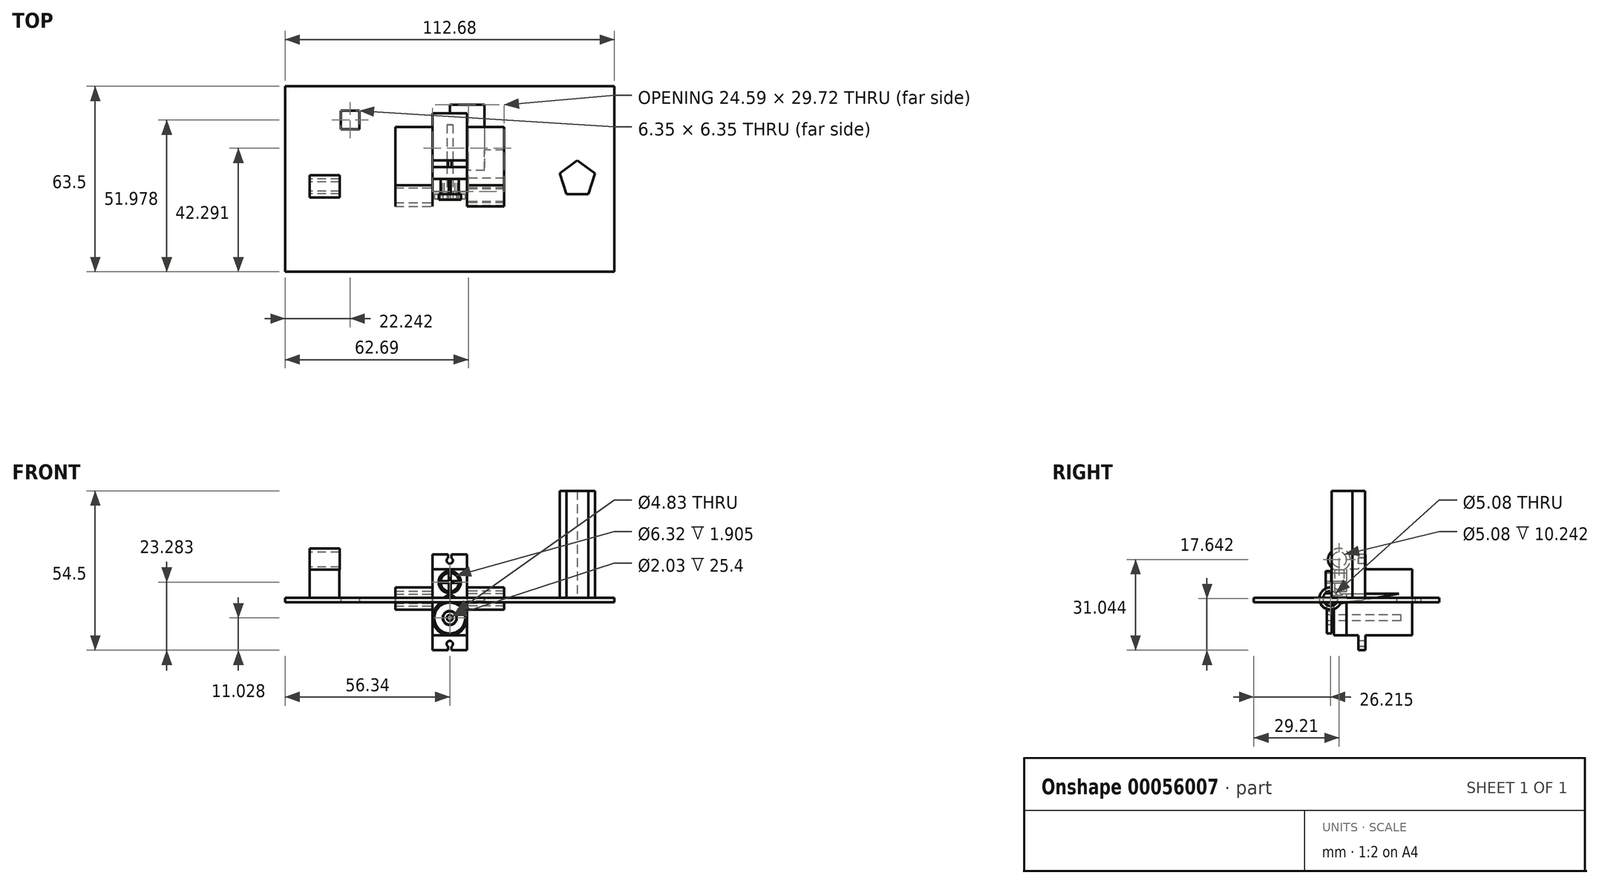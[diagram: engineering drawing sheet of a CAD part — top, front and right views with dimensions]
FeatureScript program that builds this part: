
annotation { "Feature Type Name" : "Feature", "Feature Type Description" : "" }
export const myFeature = defineFeature(function(context is Context, id is Id, definition is map)
    precondition{}
    {
        {
            var Q0;
            Q0=qCreatedBy(makeId("Top.planeOp"),FACE);
            var sketch = newSketch(context, id + "F0", { "sketchPlane" : qUnion([Q0])});
            skLineSegment(sketch, "E0.rect.bottom", {"start": v(56.34, 31.75) * mm, "end": v(-56.34, 31.75) * mm});
            skLineSegment(sketch, "E0.rect.top", {"start": v(56.34, -31.75) * mm, "end": v(-56.34, -31.75) * mm});
            skLineSegment(sketch, "E0.rect.left", {"start": v(56.34, 31.75) * mm, "end": v(56.34, -31.75) * mm});
            skLineSegment(sketch, "E0.rect.right", {"start": v(-56.34, 31.75) * mm, "end": v(-56.34, -31.75) * mm});
            skPoint(sketch, "E0.rect.middle", {"position": v(0, 0) * mm});
            skCircle(sketch, "E1.cCircle", {"center": v(43.64, 0) * mm, "radius": 5.14 * mm, "construction": true});
            skLineSegment(sketch, "E1.0", {"start": v(47.37, -5.14) * mm, "end": v(39.9, -5.14) * mm});
            skLineSegment(sketch, "E1.1", {"start": v(39.9, -5.14) * mm, "end": v(37.6, 1.96) * mm});
            skLineSegment(sketch, "E1.2", {"start": v(37.6, 1.96) * mm, "end": v(43.64, 6.35) * mm});
            skLineSegment(sketch, "E1.3", {"start": v(43.64, 6.35) * mm, "end": v(49.68, 1.96) * mm});
            skLineSegment(sketch, "E1.4", {"start": v(49.68, 1.96) * mm, "end": v(47.37, -5.14) * mm});
            skPoint(sketch, "E1.0.midPoint", {"position": v(43.64, -5.14) * mm});
            skLineSegment(sketch, "E2.bottom", {"start": v(0, 25.4) * mm, "end": v(11.89, 25.4) * mm});
            skLineSegment(sketch, "E2.top", {"start": v(0, 2.92) * mm, "end": v(11.89, 2.92) * mm});
            skLineSegment(sketch, "E2.left", {"start": v(0, 25.4) * mm, "end": v(0, 2.92) * mm});
            skLineSegment(sketch, "E2.right", {"start": v(11.89, 25.4) * mm, "end": v(11.89, 2.92) * mm});
            skLineSegment(sketch, "E3.bottom", {"start": v(-37.27, 23.4) * mm, "end": v(-30.92, 23.4) * mm});
            skLineSegment(sketch, "E3.top", {"start": v(-37.27, 17.05) * mm, "end": v(-30.92, 17.05) * mm});
            skLineSegment(sketch, "E3.left", {"start": v(-37.27, 23.4) * mm, "end": v(-37.27, 17.05) * mm});
            skLineSegment(sketch, "E3.right", {"start": v(-30.92, 23.4) * mm, "end": v(-30.92, 17.05) * mm});
            skLineSegment(sketch, "E4", {"start": v(5.94, 25.4) * mm, "end": v(5.94, 2.92) * mm});
            skLineSegment(sketch, "E5.rect.bottom", {"start": v(-37.73, -4.12) * mm, "end": v(-47.94, -4.12) * mm});
            skLineSegment(sketch, "E5.rect.top", {"start": v(-37.73, -0.96) * mm, "end": v(-47.94, -0.96) * mm});
            skLineSegment(sketch, "E5.rect.left", {"start": v(-37.73, -4.12) * mm, "end": v(-37.73, -0.96) * mm});
            skLineSegment(sketch, "E5.rect.right", {"start": v(-47.94, -4.12) * mm, "end": v(-47.94, -0.96) * mm});
            skPoint(sketch, "E5.rect.middle", {"position": v(-42.83, -2.54) * mm});
            skSolve(sketch);
        }
        {
            var Q0;
            Q0 = qSketchRegion(id + "F0", true);
            extrude(context, id + "F1", {"entities" : qUnion([Q0]), "depth" : 1.59 * mm});
        }
        {
            var Q0;
            Q0=makeQuery(id+"F0.imprint","IMPRINT",FACE,{"disambiguationData":[TD([[makeQuery(id+"F0.imprint","IMPRINT",EDGE,{"derivedFrom":sQuery(id+"F0.wireOp",EDGE,"E1.0")}),-1.0]])]});
            extrude(context, id + "F2", {"entities" : qUnion([Q0]), "operationType" : NewBodyOperationType.ADD, "depth" : 38.1 * mm});
        }
        {
            var Q0;
            Q0=qCreatedBy(makeId("Front.planeOp"),FACE);
            var sketch = newSketch(context, id + "F3", { "sketchPlane" : qUnion([Q0])});
            skLineSegment(sketch, "E6.rect.bottom", {"start": v(5.94, 11.32) * mm, "end": v(-5.94, 11.32) * mm});
            skLineSegment(sketch, "E6.rect.top", {"start": v(5.94, -11.32) * mm, "end": v(-5.94, -11.32) * mm});
            skLineSegment(sketch, "E6.rect.left", {"start": v(5.94, 11.32) * mm, "end": v(5.94, -11.32) * mm});
            skLineSegment(sketch, "E6.rect.right", {"start": v(-5.94, 11.32) * mm, "end": v(-5.94, -11.32) * mm});
            skPoint(sketch, "E6.rect.middle", {"position": v(0, 0) * mm});
            skCircle(sketch, "E7", {"center": v(0, -5.37) * mm, "radius": 5.94 * mm});
            skCircle(sketch, "E8", {"center": v(0, -5.37) * mm, "radius": 2.3 * mm});
            skCircle(sketch, "E9", {"center": v(0, 0) * mm, "radius": 2.45 * mm});
            skSolve(sketch);
        }
        {
            var Q0;
            {var subQ0=sQuery(id+"F3.wireOp",EDGE,"E9");var subQ1=sQuery(id+"F3.wireOp",EDGE,"E7");var subQ2=makeQuery(id+"F3.imprint","INTERSECT",VERTEX,{"disambiguationData":[OD(0.0)],"derivedFrom":[subQ1,subQ0]});Q0=makeQuery(id+"F3.imprint","IMPRINT",FACE,{"disambiguationData":[TD([[makeQuery(id+"F3.imprint","IMPRINT",EDGE,{"disambiguationData":[TD([[subQ2,-1.0]])],"derivedFrom":subQ1}),-1.0]])]});}
            var Q1;
            {var subQ0=sQuery(id+"F3.wireOp",EDGE,"E9");var subQ1=sQuery(id+"F3.wireOp",EDGE,"E7");var subQ2=makeQuery(id+"F3.imprint","INTERSECT",VERTEX,{"disambiguationData":[OD(0.0)],"derivedFrom":[subQ1,subQ0]});Q1=makeQuery(id+"F3.imprint","IMPRINT",FACE,{"disambiguationData":[TD([[makeQuery(id+"F3.imprint","IMPRINT",EDGE,{"disambiguationData":[TD([[subQ2,-1.0]])],"derivedFrom":subQ1}),1.0]])]});}
            var Q2;
            Q2=makeQuery(id+"F3.imprint","IMPRINT",FACE,{"disambiguationData":[TD([[makeQuery(id+"F3.imprint","IMPRINT",EDGE,{"derivedFrom":sQuery(id+"F3.wireOp",EDGE,"E8")}),1.0]])]});
            var Q3;
            Q3=makeQuery(id+"F3.imprint","IMPRINT",FACE,{"disambiguationData":[TD([[makeQuery(id+"F3.imprint","IMPRINT",EDGE,{"derivedFrom":sQuery(id+"F3.wireOp",EDGE,"E8")}),-1.0]])]});
            extrude(context, id + "F4", {"entities" : qUnion([Q0, Q1, Q2, Q3]), "depth" : 4.32 * mm});
        }
        {
            var Q0;
            Q0=makeQuery(id+"F3.imprint","IMPRINT",FACE,{"disambiguationData":[TD([[makeQuery(id+"F3.imprint","IMPRINT",EDGE,{"derivedFrom":sQuery(id+"F3.wireOp",EDGE,"E8")}),1.0]])]});
            extrude(context, id + "F5", {"entities" : qUnion([Q0]), "operationType" : NewBodyOperationType.ADD, "depth" : 6.76 * mm});
        }
        {
            var Q0;
            {var subQ0=sQuery(id+"F3.wireOp",EDGE,"E9");var subQ1=sQuery(id+"F3.wireOp",EDGE,"E7");var subQ2=makeQuery(id+"F3.imprint","INTERSECT",VERTEX,{"disambiguationData":[OD(0.0)],"derivedFrom":[subQ1,subQ0]});Q0=makeQuery(id+"F3.imprint","IMPRINT",FACE,{"disambiguationData":[TD([[makeQuery(id+"F3.imprint","IMPRINT",EDGE,{"disambiguationData":[TD([[subQ2,-1.0]])],"derivedFrom":subQ1}),1.0]])]});}
            var Q1;
            Q1=makeQuery(id+"F3.imprint","IMPRINT",FACE,{"disambiguationData":[TD([[makeQuery(id+"F3.imprint","IMPRINT",EDGE,{"derivedFrom":sQuery(id+"F3.wireOp",EDGE,"E8")}),-1.0]])]});
            var Q2;
            Q2=makeQuery(id+"F3.imprint","IMPRINT",FACE,{"disambiguationData":[TD([[makeQuery(id+"F3.imprint","IMPRINT",EDGE,{"derivedFrom":sQuery(id+"F3.wireOp",EDGE,"E8")}),1.0]])]});
            var Q3;
            {var subQ0=sQuery(id+"F3.wireOp",EDGE,"E6.rect.left");var subQ1=sQuery(id+"F3.wireOp",EDGE,"E6.rect.top");var subQ2=makeQuery(id+"F3.imprint","INTERSECT",VERTEX,{"derivedFrom":[subQ1,subQ0]});Q3=makeQuery(id+"F3.imprint","IMPRINT",FACE,{"disambiguationData":[TD([[makeQuery(id+"F3.imprint","IMPRINT",EDGE,{"disambiguationData":[TD([[subQ2,-1.0]])],"derivedFrom":subQ1}),-1.0]])]});}
            var Q4;
            {var subQ0=sQuery(id+"F3.wireOp",EDGE,"E6.rect.right");var subQ1=sQuery(id+"F3.wireOp",EDGE,"E6.rect.top");var subQ2=makeQuery(id+"F3.imprint","INTERSECT",VERTEX,{"derivedFrom":[subQ1,subQ0]});Q4=makeQuery(id+"F3.imprint","IMPRINT",FACE,{"disambiguationData":[TD([[makeQuery(id+"F3.imprint","IMPRINT",EDGE,{"disambiguationData":[TD([[subQ2,1.0]])],"derivedFrom":subQ1}),-1.0]])]});}
            var Q5;
            {var subQ1=sQuery(id+"F3.wireOp",EDGE,"E6.rect.bottom");Q5=makeQuery(id+"F3.imprint","IMPRINT",FACE,{"disambiguationData":[TD([[makeQuery(id+"F3.imprint","IMPRINT",EDGE,{"derivedFrom":subQ1}),1.0]])]});}
            var Q6;
            {var subQ0=sQuery(id+"F3.wireOp",EDGE,"E9");var subQ1=sQuery(id+"F3.wireOp",EDGE,"E7");var subQ2=makeQuery(id+"F3.imprint","INTERSECT",VERTEX,{"disambiguationData":[OD(0.0)],"derivedFrom":[subQ1,subQ0]});Q6=makeQuery(id+"F3.imprint","IMPRINT",FACE,{"disambiguationData":[TD([[makeQuery(id+"F3.imprint","IMPRINT",EDGE,{"disambiguationData":[TD([[subQ2,-1.0]])],"derivedFrom":subQ1}),-1.0]])]});}
            extrude(context, id + "F6", {"entities" : qUnion([Q0, Q1, Q2, Q3, Q4, Q5, Q6]), "operationType" : NewBodyOperationType.ADD, "oppositeDirection" : true, "depth" : 22.48 * mm});
        }
        {
            var Q0;
            Q0=makeQuery(id+"F6.opExtrude","SWEPT_FACE",FACE,{"disambiguationData":[OSD([sQuery(id+"F3.wireOp",EDGE,"E6.rect.bottom")])]});
            var sketch = newSketch(context, id + "F7", { "sketchPlane" : qUnion([Q0])});
            skLineSegment(sketch, "E10", {"start": v(-5.94, 4.06) * mm, "end": v(5.94, 4.06) * mm});
            skLineSegment(sketch, "E11", {"start": v(5.94, 4.06) * mm, "end": v(5.94, 6.4) * mm});
            skLineSegment(sketch, "E12", {"start": v(5.94, 6.4) * mm, "end": v(-5.94, 6.4) * mm});
            skLineSegment(sketch, "E13", {"start": v(-5.94, 6.4) * mm, "end": v(-5.94, 4.06) * mm});
            skSolve(sketch);
        }
        {
            var Q0;
            Q0=makeQuery(id+"F7.imprint","IMPRINT",FACE,{"disambiguationData":[TD([[makeQuery(id+"F7.imprint","IMPRINT",EDGE,{"derivedFrom":sQuery(id+"F7.wireOp",EDGE,"E10")}),1.0]])]});
            extrude(context, id + "F8", {"entities" : qUnion([Q0]), "operationType" : NewBodyOperationType.ADD, "depth" : 5.08 * mm});
        }
        {
            var Q0;
            Q0=makeQuery(id+"F8.opExtrude","SWEPT_FACE",FACE,{"disambiguationData":[OSD([sQuery(id+"F7.wireOp",EDGE,"E10")])]});
            var sketch = newSketch(context, id + "F9", { "sketchPlane" : qUnion([Q0])});
            skCircle(sketch, "E14", {"center": v(0, 14.29) * mm, "radius": 1.07 * mm});
            skLineSegment(sketch, "E15.bottom", {"start": v(-0.52, 16.4) * mm, "end": v(0.62, 16.4) * mm});
            skLineSegment(sketch, "E15.top", {"start": v(-0.52, 15) * mm, "end": v(0.62, 15) * mm});
            skLineSegment(sketch, "E15.left", {"start": v(-0.52, 16.4) * mm, "end": v(-0.52, 15) * mm});
            skLineSegment(sketch, "E15.right", {"start": v(0.62, 16.4) * mm, "end": v(0.62, 15) * mm});
            skSolve(sketch);
        }
        {
            var Q0;
            Q0 = qSketchRegion(id + "F9", true);
            extrude(context, id + "F10", {"entities" : qUnion([Q0]), "operationType" : NewBodyOperationType.REMOVE, "oppositeDirection" : true, "depth" : 2.48 * mm});
        }
        {
            var Q0;
            Q0=makeQuery(id+"F6.opExtrude","SWEPT_FACE",FACE,{"disambiguationData":[OSD([sQuery(id+"F3.wireOp",EDGE,"E6.rect.top")])]});
            var sketch = newSketch(context, id + "F11", { "sketchPlane" : qUnion([Q0])});
            skLineSegment(sketch, "E16", {"start": v(-5.94, -4.06) * mm, "end": v(5.94, -4.06) * mm});
            skLineSegment(sketch, "E17", {"start": v(5.94, -4.06) * mm, "end": v(5.94, -6.4) * mm});
            skLineSegment(sketch, "E18", {"start": v(5.94, -6.4) * mm, "end": v(-5.94, -6.4) * mm});
            skLineSegment(sketch, "E19", {"start": v(-5.94, -6.4) * mm, "end": v(-5.94, -4.06) * mm});
            skSolve(sketch);
        }
        {
            var Q0;
            Q0=makeQuery(id+"F11.imprint","IMPRINT",FACE,{"disambiguationData":[TD([[makeQuery(id+"F11.imprint","IMPRINT",EDGE,{"derivedFrom":sQuery(id+"F11.wireOp",EDGE,"E16")}),-1.0]])]});
            extrude(context, id + "F12", {"entities" : qUnion([Q0]), "operationType" : NewBodyOperationType.ADD, "depth" : 5.08 * mm});
        }
        {
            var Q0;
            Q0=makeQuery(id+"F12.opExtrude","SWEPT_FACE",FACE,{"disambiguationData":[OSD([sQuery(id+"F11.wireOp",EDGE,"E16")])]});
            var sketch = newSketch(context, id + "F13", { "sketchPlane" : qUnion([Q0])});
            skLineSegment(sketch, "E20", {"start": v(5.94, -16.4) * mm, "end": v(0.52, -16.4) * mm});
            skLineSegment(sketch, "E21", {"start": v(0.52, -16.4) * mm, "end": v(-0.62, -16.4) * mm});
            skLineSegment(sketch, "E22", {"start": v(0.52, -16.4) * mm, "end": v(0.52, -15.22) * mm});
            skArc(sketch, "E23", {"start": v(0.52, -15.22) * mm, "mid": v(0.06, -13.22) * mm, "end": v(-0.62, -15.15) * mm});
            skLineSegment(sketch, "E24", {"start": v(-0.62, -16.4) * mm, "end": v(-0.62, -15.15) * mm});
            skPoint(sketch, "E25.orphan", {"position": v(0.52, -15) * mm});
            skPoint(sketch, "E26.orphan", {"position": v(-0.62, -15) * mm});
            skSolve(sketch);
        }
        {
            var Q0;
            Q0 = qSketchRegion(id + "F13", true);
            extrude(context, id + "F14", {"entities" : qUnion([Q0]), "operationType" : NewBodyOperationType.REMOVE, "oppositeDirection" : true, "depth" : 25.4 * mm});
        }
        {
            var Q0;
            Q0=makeQuery(id+"F5.opExtrude","CAP_FACE",FACE,{"disambiguationData":[OSD([sQuery(id+"F3.wireOp",EDGE,"E8")])],"isStart":false});
            var sketch = newSketch(context, id + "F15", { "sketchPlane" : qUnion([Q0])});
            skCircle(sketch, "E27", {"center": v(0, -5.37) * mm, "radius": 1.02 * mm});
            skSolve(sketch);
        }
        {
            var Q0;
            Q0 = qSketchRegion(id + "F15", true);
            extrude(context, id + "F16", {"entities" : qUnion([Q0]), "operationType" : NewBodyOperationType.REMOVE, "oppositeDirection" : true, "depth" : 25.4 * mm});
        }
        {
            var Q0;
            {var subQ0=sQuery(id+"F3.wireOp",EDGE,"E6.rect.right");var subQ1=sQuery(id+"F3.wireOp",EDGE,"E6.rect.left");var subQ2=sQuery(id+"F3.wireOp",EDGE,"E6.rect.bottom");var subQ3=makeQuery(id+"F6.opExtrude","CAP_FACE",FACE,{"disambiguationData":[OSD([subQ2,sQuery(id+"F3.wireOp",EDGE,"E6.rect.top"),subQ1,subQ0])],"isStart":true});Q0=makeQuery(id+"F6.boolean.opBoolean","SPLIT",FACE,{"disambiguationData":[TD([makeQuery(id+"F4.opExtrude","SWEPT_FACE",FACE,{"disambiguationData":[OSD([sQuery(id+"F3.wireOp",EDGE,"E7")])]}),makeQuery(id+"F4.opExtrude","SWEPT_FACE",FACE,{"disambiguationData":[OSD([sQuery(id+"F3.wireOp",EDGE,"E9")])]}),makeQuery(id+"F6.opExtrude","SWEPT_FACE",FACE,{"disambiguationData":[OSD([subQ2])]}),subQ3,makeQuery(id+"F6.opExtrude","SWEPT_FACE",FACE,{"disambiguationData":[OSD([subQ1])]}),makeQuery(id+"F6.opExtrude","SWEPT_FACE",FACE,{"disambiguationData":[OSD([subQ0])]})])],"derivedFrom":subQ3});}
            var sketch = newSketch(context, id + "F17", { "sketchPlane" : qUnion([Q0])});
            skPoint(sketch, "E28.endSnap0", {"position": v(0, 2.45) * mm});
            skLineSegment(sketch, "E29", {"start": v(0, 10.05) * mm, "end": v(-0.32, 10.05) * mm});
            skLineSegment(sketch, "E30", {"start": v(0, 10.05) * mm, "end": v(0.32, 10.05) * mm});
            skLineSegment(sketch, "E31", {"start": v(-3.16, 6.88) * mm, "end": v(-3.16, 7.2) * mm});
            skLineSegment(sketch, "E32", {"start": v(-3.16, 6.88) * mm, "end": v(-3.16, 6.57) * mm});
            skLineSegment(sketch, "E33", {"start": v(-3.16, 7.2) * mm, "end": v(-0.32, 7.2) * mm});
            skLineSegment(sketch, "E34", {"start": v(-0.32, 7.2) * mm, "end": v(-0.32, 10.05) * mm});
            skLineSegment(sketch, "E35", {"start": v(0.32, 10.05) * mm, "end": v(0.32, 7.2) * mm});
            skLineSegment(sketch, "E36", {"start": v(0.32, 7.2) * mm, "end": v(3.16, 7.2) * mm});
            skLineSegment(sketch, "E37", {"start": v(3.16, 7.2) * mm, "end": v(3.16, 6.57) * mm});
            skLineSegment(sketch, "E38", {"start": v(3.16, 6.57) * mm, "end": v(0.32, 6.57) * mm});
            skLineSegment(sketch, "E39", {"start": v(0.32, 6.57) * mm, "end": v(0.32, 3.72) * mm});
            skLineSegment(sketch, "E40", {"start": v(0.32, 3.72) * mm, "end": v(-0.32, 3.72) * mm});
            skLineSegment(sketch, "E41", {"start": v(-0.32, 3.72) * mm, "end": v(-0.32, 6.57) * mm});
            skLineSegment(sketch, "E42", {"start": v(-0.32, 6.57) * mm, "end": v(-3.16, 6.57) * mm});
            skSolve(sketch);
        }
        {
            var Q0;
            Q0 = qSketchRegion(id + "F17", true);
            extrude(context, id + "F18", {"entities" : qUnion([Q0]), "depth" : 7.11 * mm});
        }
        {
            var Q0;
            Q0=makeQuery(id+"F18.opExtrude","CAP_FACE",FACE,{"disambiguationData":[OSD([sQuery(id+"F17.wireOp",EDGE,"E29"),sQuery(id+"F17.wireOp",EDGE,"E30"),sQuery(id+"F17.wireOp",EDGE,"E31"),sQuery(id+"F17.wireOp",EDGE,"E32"),sQuery(id+"F17.wireOp",EDGE,"E33"),sQuery(id+"F17.wireOp",EDGE,"E34"),sQuery(id+"F17.wireOp",EDGE,"E35"),sQuery(id+"F17.wireOp",EDGE,"E36"),sQuery(id+"F17.wireOp",EDGE,"E37"),sQuery(id+"F17.wireOp",EDGE,"E38"),sQuery(id+"F17.wireOp",EDGE,"E39"),sQuery(id+"F17.wireOp",EDGE,"E40"),sQuery(id+"F17.wireOp",EDGE,"E41"),sQuery(id+"F17.wireOp",EDGE,"E42")])],"isStart":false});
            var sketch = newSketch(context, id + "F19", { "sketchPlane" : qUnion([Q0])});
            skCircle(sketch, "E43", {"center": v(0, 6.88) * mm, "radius": 3.16 * mm});
            skPoint(sketch, "E43.centerSnap0", {"position": v(3.16, 6.88) * mm});
            skPoint(sketch, "E43.centerSnap1", {"position": v(0, 3.72) * mm});
            skCircle(sketch, "E44", {"center": v(0, 6.88) * mm, "radius": 3.81 * mm});
            skSolve(sketch);
        }
        {
            var Q0;
            Q0 = qSketchRegion(id + "F19", true);
            extrude(context, id + "F20", {"entities" : qUnion([Q0]), "oppositeDirection" : true, "depth" : 1.9 * mm});
        }
        {
            var Q0;
            Q0=makeQuery(id+"F5.opExtrude","CAP_FACE",FACE,{"disambiguationData":[OSD([sQuery(id+"F3.wireOp",EDGE,"E8")])],"isStart":false});
            var sketch = newSketch(context, id + "F21", { "sketchPlane" : qUnion([Q0])});
            skCircle(sketch, "E45", {"center": v(0, -5.37) * mm, "radius": 2.41 * mm});
            skCircle(sketch, "E46", {"center": v(0, -5.37) * mm, "radius": 5.27 * mm});
            skSolve(sketch);
        }
        {
            var Q0;
            Q0 = qSketchRegion(id + "F21", true);
            extrude(context, id + "F22", {"entities" : qUnion([Q0]), "oppositeDirection" : true, "depth" : 1.6 * mm});
        }
        {
            var Q0;
            Q0=makeQuery(id+"F12.boolean.opBoolean","MERGE",FACE,{"derivedFrom":[makeQuery(id+"F8.boolean.opBoolean","MERGE",FACE,{"derivedFrom":[makeQuery(id+"F6.opExtrude","SWEPT_FACE",FACE,{"disambiguationData":[OSD([sQuery(id+"F3.wireOp",EDGE,"E6.rect.right")])]}),makeQuery(id+"F8.opExtrude","SWEPT_FACE",FACE,{"disambiguationData":[OSD([sQuery(id+"F7.wireOp",EDGE,"E13")])]})]}),makeQuery(id+"F12.opExtrude","SWEPT_FACE",FACE,{"disambiguationData":[OSD([sQuery(id+"F11.wireOp",EDGE,"E19")])]})]});
            var sketch = newSketch(context, id + "F23", { "sketchPlane" : qUnion([Q0])});
            skLineSegment(sketch, "E47", {"start": v(-17.9, 2.81) * mm, "end": v(2.06, 2.81) * mm});
            skCircle(sketch, "E48", {"center": v(5.53, 1.24) * mm, "radius": 3.81 * mm});
            skLineSegment(sketch, "E49", {"start": v(-17.9, 2.81) * mm, "end": v(2.06, -0.33) * mm});
            skCircle(sketch, "E50", {"center": v(5.53, 1.24) * mm, "radius": 2.54 * mm});
            skSolve(sketch);
        }
        {
            var Q0;
            Q0 = qSketchRegion(id + "F23", true);
            extrude(context, id + "F24", {"entities" : qUnion([Q0]), "depth" : 12.7 * mm});
        }
        {
            var Q0;
            Q0=makeQuery(id+"F12.boolean.opBoolean","MERGE",FACE,{"derivedFrom":[makeQuery(id+"F8.boolean.opBoolean","MERGE",FACE,{"derivedFrom":[makeQuery(id+"F6.opExtrude","SWEPT_FACE",FACE,{"disambiguationData":[OSD([sQuery(id+"F3.wireOp",EDGE,"E6.rect.left")])]}),makeQuery(id+"F8.opExtrude","SWEPT_FACE",FACE,{"disambiguationData":[OSD([sQuery(id+"F7.wireOp",EDGE,"E11")])]})]}),makeQuery(id+"F12.opExtrude","SWEPT_FACE",FACE,{"disambiguationData":[OSD([sQuery(id+"F11.wireOp",EDGE,"E17")])]})]});
            var sketch = newSketch(context, id + "F25", { "sketchPlane" : qUnion([Q0])});
            skCircle(sketch, "E51", {"center": v(-5.5, 1.29) * mm, "radius": 2.54 * mm});
            skCircle(sketch, "E52", {"center": v(-5.5, 1.29) * mm, "radius": 3.79 * mm});
            skLineSegment(sketch, "E53", {"start": v(-2.07, 2.88) * mm, "end": v(17.84, 2.88) * mm});
            skLineSegment(sketch, "E54", {"start": v(17.84, 2.88) * mm, "end": v(-2.11, -0.4) * mm});
            skSolve(sketch);
        }
        {
            var Q0;
            Q0 = qSketchRegion(id + "F25", true);
            extrude(context, id + "F26", {"entities" : qUnion([Q0]), "operationType" : NewBodyOperationType.ADD, "depth" : 12.7 * mm});
        }
        {
            var Q0;
            Q0=makeQuery(id+"F0.imprint","IMPRINT",FACE,{"disambiguationData":[TD([[makeQuery(id+"F0.imprint","IMPRINT",EDGE,{"derivedFrom":sQuery(id+"F0.wireOp",EDGE,"E5.rect.bottom")}),-1.0]])]});
            extrude(context, id + "F27", {"entities" : qUnion([Q0]), "operationType" : NewBodyOperationType.ADD, "depth" : 11.18 * mm});
        }
        {
            var Q0;
            Q0=makeQuery(id+"F27.opExtrude","SWEPT_FACE",FACE,{"disambiguationData":[OSD([sQuery(id+"F0.wireOp",EDGE,"E5.rect.right")])]});
            var sketch = newSketch(context, id + "F28", { "sketchPlane" : qUnion([Q0])});
            skCircle(sketch, "E55", {"center": v(2.54, 14.64) * mm, "radius": 2.54 * mm});
            skCircle(sketch, "E56", {"center": v(2.54, 14.64) * mm, "radius": 3.81 * mm});
            skSolve(sketch);
        }
        {
            var Q0;
            Q0=makeQuery(id+"F28.imprint","IMPRINT",FACE,{"disambiguationData":[TD([[makeQuery(id+"F28.imprint","IMPRINT",EDGE,{"derivedFrom":sQuery(id+"F28.wireOp",EDGE,"E55")}),-1.0]])]});
            extrude(context, id + "F29", {"entities" : qUnion([Q0]), "operationType" : NewBodyOperationType.ADD, "oppositeDirection" : true, "depth" : 10.24 * mm});
        }
    });
